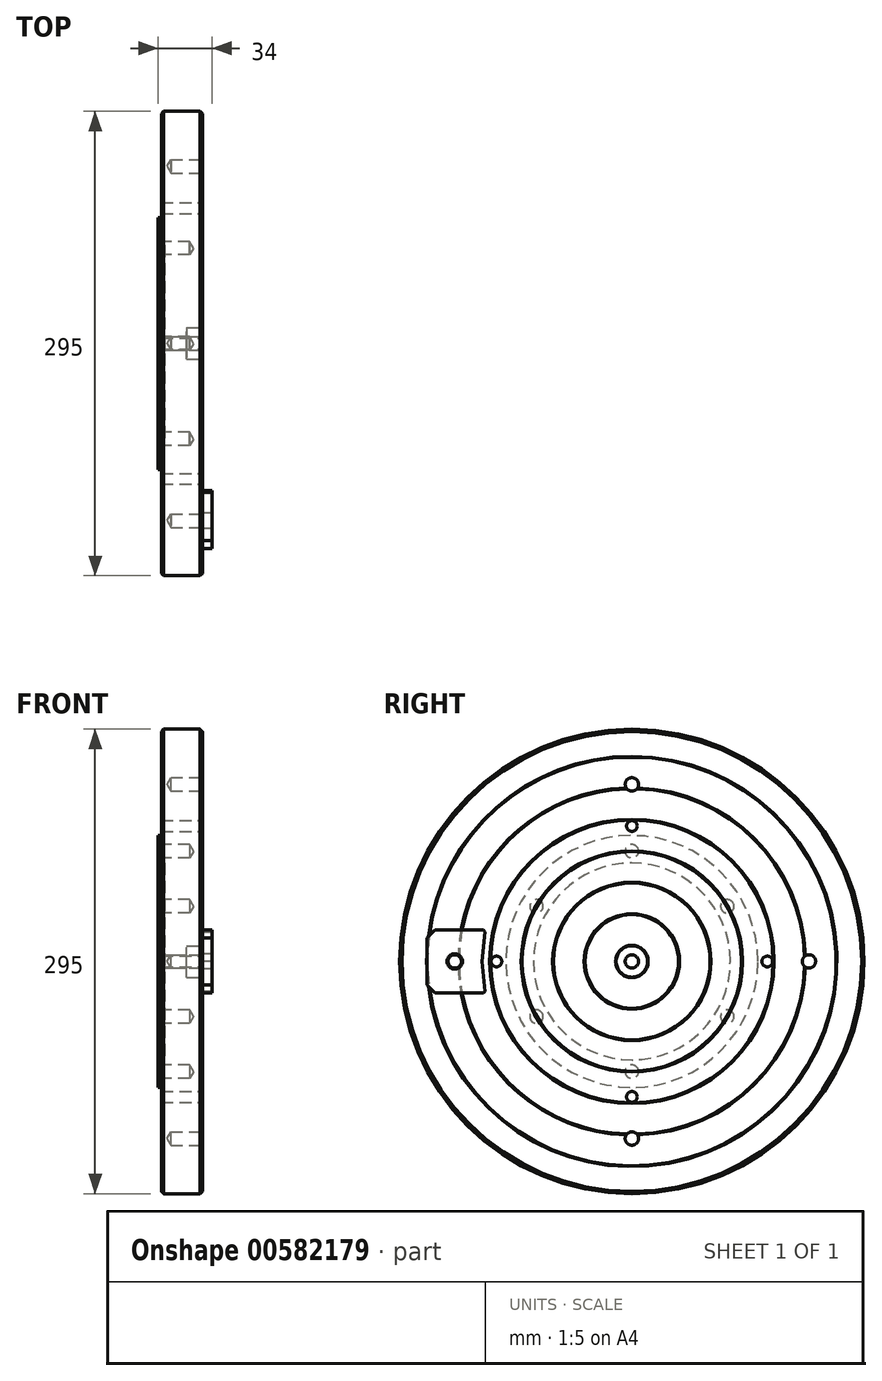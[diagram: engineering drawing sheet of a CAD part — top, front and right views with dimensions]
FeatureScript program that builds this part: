
annotation { "Feature Type Name" : "Feature", "Feature Type Description" : "" }
export const myFeature = defineFeature(function(context is Context, id is Id, definition is map)
    precondition{}
    {
        {
            var Q0;
            Q0=qCreatedBy(makeId("Front.planeOp"),FACE);
            var sketch = newSketch(context, id + "F0", { "sketchPlane" : qUnion([Q0])});
            skLineSegment(sketch, "E0", {"start": v(0, 62.5) * mm, "end": v(4, 62.5) * mm});
            skLineSegment(sketch, "E1", {"start": v(4, 62.5) * mm, "end": v(4, 0) * mm});
            skLineSegment(sketch, "E2", {"start": v(4, 0) * mm, "end": v(28, 0) * mm});
            skLineSegment(sketch, "E3", {"start": v(28, 0) * mm, "end": v(28, 147.5) * mm});
            skLineSegment(sketch, "E4", {"start": v(28, 147.5) * mm, "end": v(0, 147.5) * mm});
            skLineSegment(sketch, "E5", {"start": v(0, 147.5) * mm, "end": v(0, 62.5) * mm});
            skLineSegment(sketch, "E6", {"start": v(2, 147.5) * mm, "end": v(2, 80) * mm});
            skLineSegment(sketch, "E7", {"start": v(2, 80) * mm, "end": v(0, 80) * mm});
            skSolve(sketch);
        }
        {
            var Q0;
            {var subQ1=sQuery(id+"F0.wireOp",EDGE,"E0");Q0=makeQuery(id+"F0.imprint","IMPRINT",FACE,{"disambiguationData":[TD([[makeQuery(id+"F0.imprint","IMPRINT",EDGE,{"derivedFrom":subQ1}),1.0]])]});}
            var Q1;
            Q1=sQuery(id+"F0.wireOp",EDGE,"E2");
            revolve(context, id + "F1", {"entities" : qUnion([Q0]), "axis" : qUnion([Q1]), "revolveType" : RevolveType.FULL});
        }
        {
            var Q0;
            Q0=makeQuery(id+"F1.opRevolve","SWEPT_FACE",FACE,{"disambiguationData":[OSD([sQuery(id+"F0.wireOp",EDGE,"E5")])]});
            var sketch = newSketch(context, id + "F2", { "sketchPlane" : qUnion([Q0])});
            skPoint(sketch, "E8", {"position": v(0, 70) * mm});
            skPoint(sketch, "E9.1.0", {"position": v(-60.62, 35) * mm});
            skPoint(sketch, "E9.2.0", {"position": v(-60.62, -35) * mm});
            skPoint(sketch, "E9.3.0", {"position": v(0, -70) * mm});
            skPoint(sketch, "E9.4.0", {"position": v(60.62, -35) * mm});
            skPoint(sketch, "E9.5.0", {"position": v(60.62, 35) * mm});
            skPoint(sketch, "E9.center", {"position": v(0, 0) * mm});
            skSolve(sketch);
        }
        {
            var Q0;
            Q0=sQuery(id+"F2.wireOp",VERTEX,"E8");
            var Q1;
            Q1=sQuery(id+"F2.wireOp",VERTEX,"E9.5.0");
            var Q2;
            Q2=sQuery(id+"F2.wireOp",VERTEX,"E9.4.0");
            var Q3;
            Q3=sQuery(id+"F2.wireOp",VERTEX,"E9.3.0");
            var Q4;
            Q4=sQuery(id+"F2.wireOp",VERTEX,"E9.2.0");
            var Q5;
            Q5=sQuery(id+"F2.wireOp",VERTEX,"E9.1.0");
            var Q6;
            Q6=makeQuery(id+"F1.opRevolve","SWEPT_BODY",BODY,{"disambiguationData":[OSD([sQuery(id+"F0.wireOp",EDGE,"E0"),sQuery(id+"F0.wireOp",EDGE,"E1"),sQuery(id+"F0.wireOp",EDGE,"E2"),sQuery(id+"F0.wireOp",EDGE,"E3"),sQuery(id+"F0.wireOp",EDGE,"E4"),sQuery(id+"F0.wireOp",EDGE,"E5"),sQuery(id+"F0.wireOp",EDGE,"E6"),sQuery(id+"F0.wireOp",EDGE,"E7")])]});
            hole(context, id + "F3", {"style" : HoleStyle.SIMPLE, "endStyle" : HoleEndStyle.BLIND, "standardTappedOrClearance" : lookupTablePath({ "standard" : "ISO", "engagement" : "75%", "pitch" : "1.5 mm", "size" : "M10", "type" : "Tapped" }), "standardBlindInLast" : lookupTablePath({ "standard" : "ISO", "engagement" : "75%", "pitch" : "1.5 mm", "size" : "M10", "type" : "Tapped" }), "holeDiameter" : 8.5 * mm, "showTappedDepth" : true, "holeDepth" : 20 * mm, "tappedDepth" : 15.5 * mm, "tapClearance" : 3, "locations" : qUnion([Q0, Q1, Q2, Q3, Q4, Q5]), "scope" : qUnion([Q6]), "majorDiameter" : 10 * mm});
        }
        {
            var Q0;
            Q0=qCreatedBy(makeId("Front.planeOp"),FACE);
            var sketch = newSketch(context, id + "F4", { "sketchPlane" : qUnion([Q0])});
            skLineSegment(sketch, "E10", {"start": v(28, 10.29) * mm, "end": v(27.5, 10) * mm});
            skLineSegment(sketch, "E11", {"start": v(27.5, 10) * mm, "end": v(28, 9.71) * mm});
            skLineSegment(sketch, "E12", {"start": v(28, 10.29) * mm, "end": v(28, 9.71) * mm});
            skLineSegment(sketch, "E13", {"start": v(27.5, 10) * mm, "end": v(28, 10) * mm, "construction": true});
            skLineSegment(sketch, "E14.0.1.0", {"start": v(28, 30.29) * mm, "end": v(27.5, 30) * mm});
            skLineSegment(sketch, "E14.0.1.1", {"start": v(28, 30.29) * mm, "end": v(28, 29.71) * mm});
            skLineSegment(sketch, "E14.0.1.2", {"start": v(27.5, 30) * mm, "end": v(28, 29.71) * mm});
            skLineSegment(sketch, "E14.0.2.0", {"start": v(28, 50.29) * mm, "end": v(27.5, 50) * mm});
            skLineSegment(sketch, "E14.0.2.1", {"start": v(28, 50.29) * mm, "end": v(28, 49.71) * mm});
            skLineSegment(sketch, "E14.0.2.2", {"start": v(27.5, 50) * mm, "end": v(28, 49.71) * mm});
            skLineSegment(sketch, "E14.0.3.0", {"start": v(28, 70.29) * mm, "end": v(27.5, 70) * mm});
            skLineSegment(sketch, "E14.0.3.1", {"start": v(28, 70.29) * mm, "end": v(28, 69.71) * mm});
            skLineSegment(sketch, "E14.0.3.2", {"start": v(27.5, 70) * mm, "end": v(28, 69.71) * mm});
            skLineSegment(sketch, "E14.0.4.0", {"start": v(28, 90.29) * mm, "end": v(27.5, 90) * mm});
            skLineSegment(sketch, "E14.0.4.1", {"start": v(28, 90.29) * mm, "end": v(28, 89.71) * mm});
            skLineSegment(sketch, "E14.0.4.2", {"start": v(27.5, 90) * mm, "end": v(28, 89.71) * mm});
            skLineSegment(sketch, "E14.direction2", {"start": v(27.5, 10) * mm, "end": v(27.5, 30) * mm, "construction": true});
            skLineSegment(sketch, "E15.0.0.5", {"start": v(28, 110.29) * mm, "end": v(27.5, 110) * mm});
            skLineSegment(sketch, "E15.3.0.5", {"start": v(28, 110.29) * mm, "end": v(28, 109.71) * mm});
            skLineSegment(sketch, "E15.6.0.5", {"start": v(27.5, 110) * mm, "end": v(28, 109.71) * mm});
            skLineSegment(sketch, "E15.0.0.6", {"start": v(28, 130.29) * mm, "end": v(27.5, 130) * mm});
            skLineSegment(sketch, "E15.3.0.6", {"start": v(28, 130.29) * mm, "end": v(28, 129.71) * mm});
            skLineSegment(sketch, "E15.6.0.6", {"start": v(27.5, 130) * mm, "end": v(28, 129.71) * mm});
            skLineSegment(sketch, "E15.0.0.7", {"start": v(28, 150.29) * mm, "end": v(27.5, 150) * mm});
            skLineSegment(sketch, "E15.3.0.7", {"start": v(28, 150.29) * mm, "end": v(28, 149.71) * mm});
            skLineSegment(sketch, "E15.6.0.7", {"start": v(27.5, 150) * mm, "end": v(28, 149.71) * mm});
            skLineSegment(sketch, "E15.0.0.8", {"start": v(28, 170.29) * mm, "end": v(27.5, 170) * mm});
            skLineSegment(sketch, "E15.3.0.8", {"start": v(28, 170.29) * mm, "end": v(28, 169.71) * mm});
            skLineSegment(sketch, "E15.6.0.8", {"start": v(27.5, 170) * mm, "end": v(28, 169.71) * mm});
            skLineSegment(sketch, "E15.0.0.9", {"start": v(28, 190.29) * mm, "end": v(27.5, 190) * mm});
            skLineSegment(sketch, "E15.3.0.9", {"start": v(28, 190.29) * mm, "end": v(28, 189.71) * mm});
            skLineSegment(sketch, "E15.6.0.9", {"start": v(27.5, 190) * mm, "end": v(28, 189.71) * mm});
            skLineSegment(sketch, "E16.0.0.10", {"start": v(28, 210.29) * mm, "end": v(27.5, 210) * mm});
            skLineSegment(sketch, "E16.3.0.10", {"start": v(28, 210.29) * mm, "end": v(28, 209.71) * mm});
            skLineSegment(sketch, "E16.6.0.10", {"start": v(27.5, 210) * mm, "end": v(28, 209.71) * mm});
            skLineSegment(sketch, "E16.0.0.11", {"start": v(28, 230.29) * mm, "end": v(27.5, 230) * mm});
            skLineSegment(sketch, "E16.3.0.11", {"start": v(28, 230.29) * mm, "end": v(28, 229.71) * mm});
            skLineSegment(sketch, "E16.6.0.11", {"start": v(27.5, 230) * mm, "end": v(28, 229.71) * mm});
            skLineSegment(sketch, "E16.0.0.12", {"start": v(28, 250.29) * mm, "end": v(27.5, 250) * mm});
            skLineSegment(sketch, "E16.3.0.12", {"start": v(28, 250.29) * mm, "end": v(28, 249.71) * mm});
            skLineSegment(sketch, "E16.6.0.12", {"start": v(27.5, 250) * mm, "end": v(28, 249.71) * mm});
            skLineSegment(sketch, "E16.0.0.13", {"start": v(28, 270.29) * mm, "end": v(27.5, 270) * mm});
            skLineSegment(sketch, "E16.3.0.13", {"start": v(28, 270.29) * mm, "end": v(28, 269.71) * mm});
            skLineSegment(sketch, "E16.6.0.13", {"start": v(27.5, 270) * mm, "end": v(28, 269.71) * mm});
            skLineSegment(sketch, "E17", {"start": v(28, 0) * mm, "end": v(0, 0) * mm, "construction": true});
            skSolve(sketch);
        }
        {
            var Q0;
            Q0=qSketchRegion(id+"F4",true);
            var Q1;
            Q1=sQuery(id+"F4.wireOp",EDGE,"E17");
            revolve(context, id + "F5", {"operationType" : NewBodyOperationType.REMOVE, "entities" : qUnion([Q0]), "axis" : qUnion([Q1]), "revolveType" : RevolveType.FULL, "oppositeDirection" : true});
        }
        {
            var Q0;
            Q0=makeQuery(id+"F1.opRevolve","SWEPT_EDGE",EDGE,{"disambiguationData":[OSD([sQuery(id+"F0.wireOp",EDGE,"E3"),sQuery(id+"F0.wireOp",EDGE,"E4")])]});
            var Q1;
            Q1=makeQuery(id+"F1.opRevolve","SWEPT_EDGE",EDGE,{"disambiguationData":[OSD([sQuery(id+"F0.wireOp",EDGE,"E4"),sQuery(id+"F0.wireOp",EDGE,"E6")])]});
            chamfer(context, id + "F6", {"entities" : qUnion([Q0, Q1]), "width" : 1.5 * mm, "tangentPropagation" : true});
        }
        {
            var Q0;
            Q0=makeQuery(id+"F1.opRevolve","SWEPT_FACE",FACE,{"disambiguationData":[OSD([sQuery(id+"F0.wireOp",EDGE,"E3")])]});
            var sketch = newSketch(context, id + "F7", { "sketchPlane" : qUnion([Q0])});
            skPoint(sketch, "E18", {"position": v(0, 86) * mm});
            skPoint(sketch, "E19.1.0", {"position": v(-86, 0) * mm});
            skPoint(sketch, "E19.2.0", {"position": v(0, -86) * mm});
            skPoint(sketch, "E19.3.0", {"position": v(86, 0) * mm});
            skPoint(sketch, "E19.center", {"position": v(0, 0) * mm});
            skSolve(sketch);
        }
        {
            var Q0;
            Q0=sQuery(id+"F7.wireOp",VERTEX,"E18");
            var Q1;
            Q1=sQuery(id+"F7.wireOp",VERTEX,"E19.3.0");
            var Q2;
            Q2=sQuery(id+"F7.wireOp",VERTEX,"E19.2.0");
            var Q3;
            Q3=sQuery(id+"F7.wireOp",VERTEX,"E19.1.0");
            var Q4;
            Q4=makeQuery(id+"F1.opRevolve","SWEPT_BODY",BODY,{"disambiguationData":[OSD([sQuery(id+"F0.wireOp",EDGE,"E0"),sQuery(id+"F0.wireOp",EDGE,"E1"),sQuery(id+"F0.wireOp",EDGE,"E2"),sQuery(id+"F0.wireOp",EDGE,"E3"),sQuery(id+"F0.wireOp",EDGE,"E4"),sQuery(id+"F0.wireOp",EDGE,"E5"),sQuery(id+"F0.wireOp",EDGE,"E6"),sQuery(id+"F0.wireOp",EDGE,"E7")])]});
            hole(context, id + "F8", {"style" : HoleStyle.SIMPLE, "endStyle" : HoleEndStyle.THROUGH, "standardTappedOrClearance" : lookupTablePath({ "standard" : "ISO", "engagement" : "75%", "pitch" : "1.25 mm", "size" : "M8", "type" : "Tapped" }), "standardBlindInLast" : lookupTablePath({ "standard" : "ISO", "engagement" : "75%", "pitch" : "1.25 mm", "size" : "M8", "type" : "Tapped" }), "holeDiameter" : 6.8 * mm, "showTappedDepth" : true, "isTappedThrough" : true, "tappedDepth" : 16 * mm, "tapClearance" : 3, "startFromSketch" : true, "locations" : qUnion([Q0, Q1, Q2, Q3]), "scope" : qUnion([Q4]), "majorDiameter" : 8 * mm});
        }
        {
            var Q0;
            Q0=makeQuery(id+"F1.opRevolve","SWEPT_FACE",FACE,{"disambiguationData":[OSD([sQuery(id+"F0.wireOp",EDGE,"E3")])]});
            var sketch = newSketch(context, id + "F9", { "sketchPlane" : qUnion([Q0])});
            skPoint(sketch, "E20", {"position": v(0, 0) * mm});
            skSolve(sketch);
        }
        {
            var Q0;
            Q0=sQuery(id+"F9.wireOp",VERTEX,"E20");
            var Q1;
            Q1=makeQuery(id+"F1.opRevolve","SWEPT_BODY",BODY,{"disambiguationData":[OSD([sQuery(id+"F0.wireOp",EDGE,"E0"),sQuery(id+"F0.wireOp",EDGE,"E1"),sQuery(id+"F0.wireOp",EDGE,"E2"),sQuery(id+"F0.wireOp",EDGE,"E3"),sQuery(id+"F0.wireOp",EDGE,"E4"),sQuery(id+"F0.wireOp",EDGE,"E5"),sQuery(id+"F0.wireOp",EDGE,"E6"),sQuery(id+"F0.wireOp",EDGE,"E7")])]});
            hole(context, id + "F10", {"style" : HoleStyle.C_BORE, "endStyle" : HoleEndStyle.THROUGH, "holeDiameter" : 8.5 * mm, "cBoreDiameter" : 20 * mm, "cBoreDepth" : 10 * mm, "isTappedThrough" : true, "tappedDepth" : 16 * mm, "tapClearance" : 3, "startFromSketch" : true, "locations" : qUnion([Q0]), "scope" : qUnion([Q1])});
        }
        {
            var Q0;
            Q0=makeQuery(id+"F5.boolean.opBoolean","SPLIT",FACE,{"disambiguationData":[TD([makeQuery(id+"F5.opRevolve","SWEPT_FACE",FACE,{"disambiguationData":[OSD([sQuery(id+"F4.wireOp",EDGE,"E15.0.0.5")])]})])],"derivedFrom":makeQuery(id+"F1.opRevolve","SWEPT_FACE",FACE,{"disambiguationData":[OSD([sQuery(id+"F0.wireOp",EDGE,"E3")])]})});
            var sketch = newSketch(context, id + "F11", { "sketchPlane" : qUnion([Q0])});
            skPoint(sketch, "E21", {"position": v(0, 112.5) * mm});
            skPoint(sketch, "E22.1.0", {"position": v(-112.5, 0) * mm});
            skPoint(sketch, "E22.2.0", {"position": v(0, -112.5) * mm});
            skPoint(sketch, "E22.3.0", {"position": v(112.5, 0) * mm});
            skPoint(sketch, "E22.center", {"position": v(0, 0) * mm});
            skSolve(sketch);
        }
        {
            var Q0;
            Q0=sQuery(id+"F11.wireOp",VERTEX,"E21");
            var Q1;
            Q1=sQuery(id+"F11.wireOp",VERTEX,"E22.3.0");
            var Q2;
            Q2=sQuery(id+"F11.wireOp",VERTEX,"E22.2.0");
            var Q3;
            Q3=sQuery(id+"F11.wireOp",VERTEX,"E22.1.0");
            var Q4;
            Q4=makeQuery(id+"F1.opRevolve","SWEPT_BODY",BODY,{"disambiguationData":[OSD([sQuery(id+"F0.wireOp",EDGE,"E0"),sQuery(id+"F0.wireOp",EDGE,"E1"),sQuery(id+"F0.wireOp",EDGE,"E2"),sQuery(id+"F0.wireOp",EDGE,"E3"),sQuery(id+"F0.wireOp",EDGE,"E4"),sQuery(id+"F0.wireOp",EDGE,"E5"),sQuery(id+"F0.wireOp",EDGE,"E6"),sQuery(id+"F0.wireOp",EDGE,"E7")])]});
            hole(context, id + "F12", {"style" : HoleStyle.SIMPLE, "endStyle" : HoleEndStyle.BLIND, "standardTappedOrClearance" : lookupTablePath({ "standard" : "ISO", "engagement" : "75%", "pitch" : "1.5 mm", "size" : "M10", "type" : "Tapped" }), "standardBlindInLast" : lookupTablePath({ "standard" : "ISO", "engagement" : "75%", "pitch" : "1.5 mm", "size" : "M10", "type" : "Tapped" }), "holeDiameter" : 8.5 * mm, "showTappedDepth" : true, "holeDepth" : 20 * mm, "isTappedThrough" : true, "tappedDepth" : 15.5 * mm, "tapClearance" : 3, "startFromSketch" : true, "locations" : qUnion([Q0, Q1, Q2, Q3]), "scope" : qUnion([Q4]), "majorDiameter" : 10 * mm});
        }
        {
            var Q0;
            Q0=makeQuery(id+"F5.boolean.opBoolean","SPLIT",FACE,{"disambiguationData":[TD([makeQuery(id+"F5.opRevolve","SWEPT_FACE",FACE,{"disambiguationData":[OSD([sQuery(id+"F4.wireOp",EDGE,"E15.0.0.5")])]})])],"derivedFrom":makeQuery(id+"F1.opRevolve","SWEPT_FACE",FACE,{"disambiguationData":[OSD([sQuery(id+"F0.wireOp",EDGE,"E3")])]})});
            var sketch = newSketch(context, id + "F13", { "sketchPlane" : qUnion([Q0])});
            skLineSegment(sketch, "E23.bottom", {"start": v(-130.16, 20) * mm, "end": v(-93.16, 20) * mm});
            skLineSegment(sketch, "E23.top", {"start": v(-130.16, -20) * mm, "end": v(-93.16, -20) * mm});
            skLineSegment(sketch, "E23.left", {"start": v(-130.16, 20) * mm, "end": v(-130.16, -20) * mm});
            skLineSegment(sketch, "E24", {"start": v(-95.28, 0) * mm, "end": v(-130.16, 0) * mm, "construction": true});
            skLineSegment(sketch, "E25", {"start": v(-93.16, 20) * mm, "end": v(-95.28, 0) * mm});
            skLineSegment(sketch, "E26", {"start": v(-95.28, 0) * mm, "end": v(-93.16, -20) * mm});
            skLineSegment(sketch, "E27", {"start": v(-130.16, 10) * mm, "end": v(-94.22, 10) * mm, "construction": true});
            skLineSegment(sketch, "E28", {"start": v(-130.16, -10) * mm, "end": v(-94.22, -10) * mm, "construction": true});
            skCircle(sketch, "E29", {"center": v(0, 0) * mm, "radius": 94.75 * mm, "construction": true});
            skPoint(sketch, "E30", {"position": v(-112.5, 0) * mm});
            skCircle(sketch, "E31", {"center": v(-112.5, 0) * mm, "radius": 4.9 * mm});
            skSolve(sketch);
        }
        {
            var Q0;
            Q0 = qSketchRegion(id + "F13", true);
            extrude(context, id + "F14", {"entities" : qUnion([Q0]), "depth" : 6 * mm, "offsetDistance" : 25 * mm});
        }
        {
            var Q0;
            Q0=makeQuery(id+"F14.opExtrude","SWEPT_EDGE",EDGE,{"disambiguationData":[OSD([sQuery(id+"F13.wireOp",EDGE,"E23.bottom"),sQuery(id+"F13.wireOp",EDGE,"E23.left")])]});
            var Q1;
            Q1=makeQuery(id+"F14.opExtrude","SWEPT_EDGE",EDGE,{"disambiguationData":[OSD([sQuery(id+"F13.wireOp",EDGE,"E23.top"),sQuery(id+"F13.wireOp",EDGE,"E23.left")])]});
            chamfer(context, id + "F15", {"entities" : qUnion([Q0, Q1]), "width" : 5 * mm, "tangentPropagation" : true});
        }
        {
            var Q0;
            Q0=makeQuery(id+"F14.opExtrude","SWEPT_EDGE",EDGE,{"disambiguationData":[OSD([sQuery(id+"F13.wireOp",EDGE,"E23.bottom"),sQuery(id+"F13.wireOp",EDGE,"E25")])]});
            var Q1;
            Q1=makeQuery(id+"F14.opExtrude","SWEPT_EDGE",EDGE,{"disambiguationData":[OSD([sQuery(id+"F13.wireOp",EDGE,"E23.top"),sQuery(id+"F13.wireOp",EDGE,"E26")])]});
            chamfer(context, id + "F16", {"entities" : qUnion([Q0, Q1]), "width" : 1 * mm, "tangentPropagation" : true});
        }
    });
